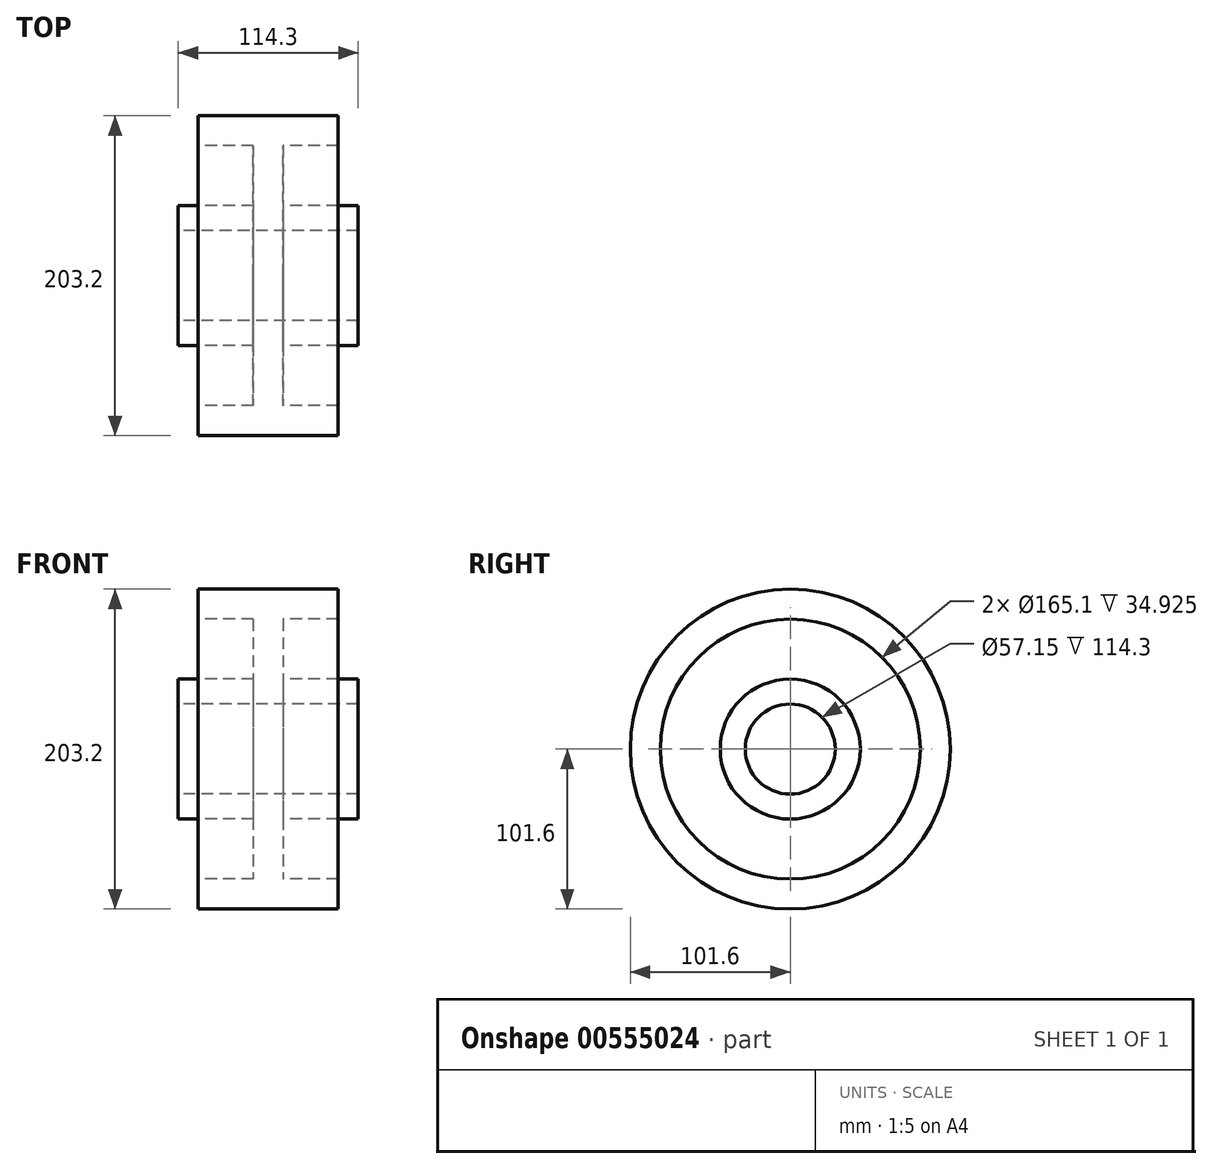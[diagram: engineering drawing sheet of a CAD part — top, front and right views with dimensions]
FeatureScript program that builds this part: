
annotation { "Feature Type Name" : "Feature", "Feature Type Description" : "" }
export const myFeature = defineFeature(function(context is Context, id is Id, definition is map)
    precondition{}
    {
        {
            var Q0;
            Q0=qCreatedBy(makeId("Front.planeOp"),FACE);
            var sketch = newSketch(context, id + "F0", { "sketchPlane" : qUnion([Q0])});
            skLineSegment(sketch, "E0", {"start": v(-372.48, 0) * mm, "end": v(354.68, 0) * mm, "construction": true});
            skLineSegment(sketch, "E1", {"start": v(0, 0) * mm, "end": v(0, 247.19) * mm, "construction": true});
            skLineSegment(sketch, "E2", {"start": v(-57.15, 28.58) * mm, "end": v(57.15, 28.58) * mm});
            skLineSegment(sketch, "E3", {"start": v(57.15, 28.58) * mm, "end": v(57.15, 44.45) * mm});
            skLineSegment(sketch, "E4", {"start": v(57.15, 44.45) * mm, "end": v(9.52, 44.45) * mm});
            skLineSegment(sketch, "E5", {"start": v(9.52, 44.45) * mm, "end": v(9.53, 82.55) * mm});
            skLineSegment(sketch, "E6", {"start": v(9.53, 82.55) * mm, "end": v(44.45, 82.55) * mm});
            skLineSegment(sketch, "E7", {"start": v(44.45, 82.55) * mm, "end": v(44.45, 101.6) * mm});
            skLineSegment(sketch, "E8", {"start": v(44.45, 101.6) * mm, "end": v(-44.45, 101.6) * mm});
            skLineSegment(sketch, "E9", {"start": v(-44.45, 101.6) * mm, "end": v(-44.45, 82.55) * mm});
            skLineSegment(sketch, "E10", {"start": v(-44.45, 82.55) * mm, "end": v(-9.53, 82.55) * mm});
            skLineSegment(sketch, "E11", {"start": v(-9.53, 82.55) * mm, "end": v(-9.52, 44.45) * mm});
            skLineSegment(sketch, "E12", {"start": v(-9.52, 44.45) * mm, "end": v(-57.15, 44.45) * mm});
            skLineSegment(sketch, "E13", {"start": v(-57.15, 44.45) * mm, "end": v(-57.15, 28.58) * mm});
            skSolve(sketch);
        }
        {
            var Q0;
            Q0 = qSketchRegion(id + "F0", true);
            var Q1;
            Q1=sQuery(id+"F0.wireOp",EDGE,"E0");
            revolve(context, id + "F1", {"entities" : qUnion([Q0]), "axis" : qUnion([Q1]), "revolveType" : RevolveType.FULL});
        }
    });
